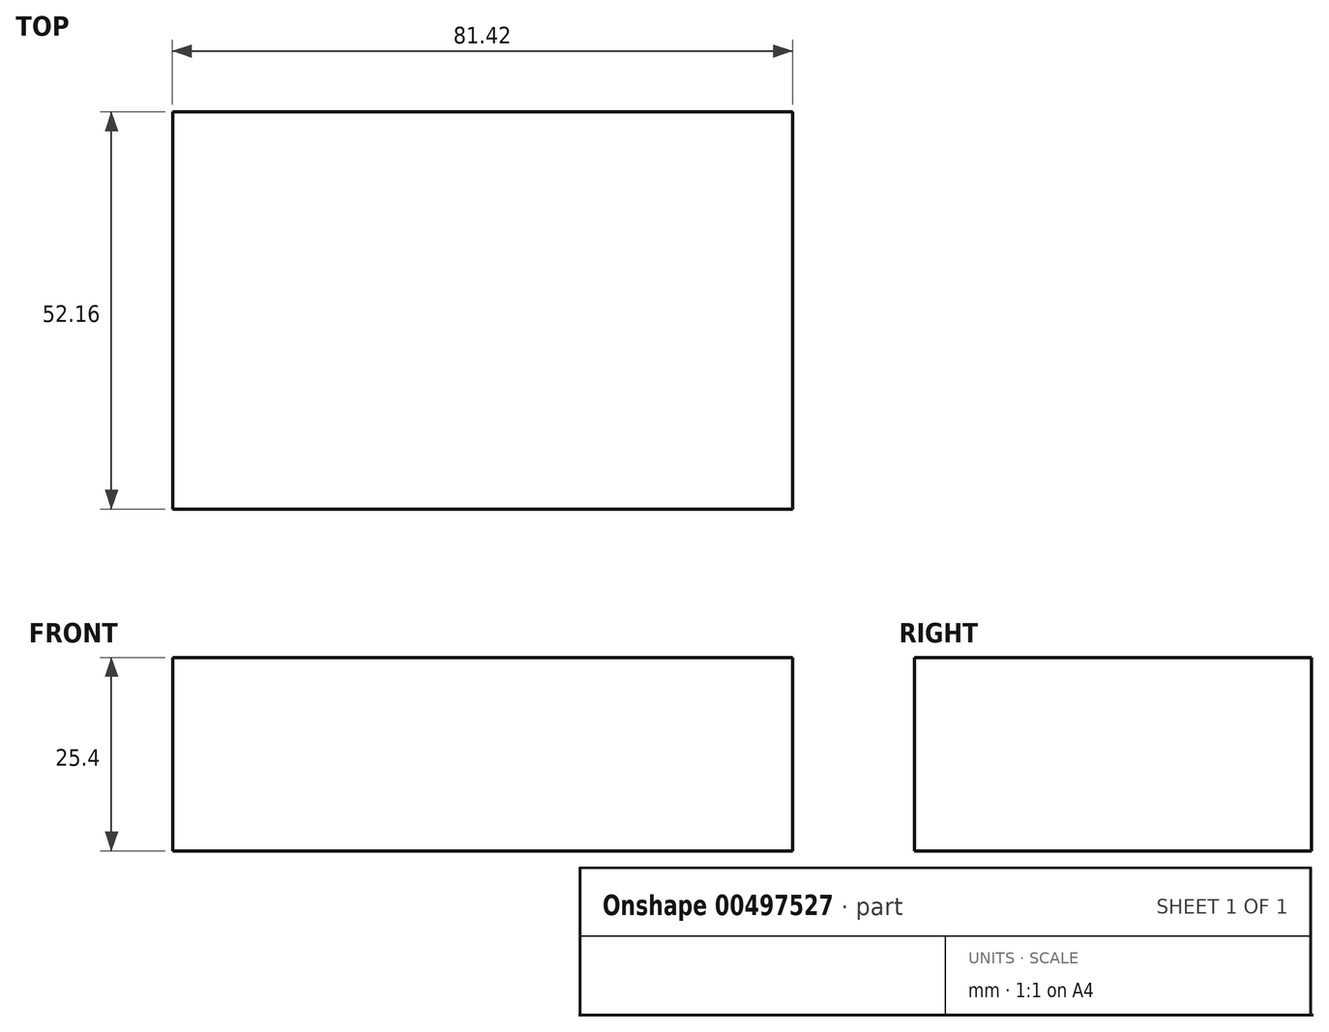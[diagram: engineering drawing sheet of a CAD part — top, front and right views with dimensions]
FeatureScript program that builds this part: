
annotation { "Feature Type Name" : "Feature", "Feature Type Description" : "" }
export const myFeature = defineFeature(function(context is Context, id is Id, definition is map)
    precondition{}
    {
        {
            var Q0;
            Q0=qCreatedBy(makeId("Top.planeOp"),FACE);
            var sketch = newSketch(context, id + "F0", { "sketchPlane" : qUnion([Q0])});
            skLineSegment(sketch, "E0.bottom", {"start": v(40.7, -26.08) * mm, "end": v(-40.7, -26.08) * mm});
            skLineSegment(sketch, "E0.top", {"start": v(40.7, 26.08) * mm, "end": v(-40.7, 26.08) * mm});
            skLineSegment(sketch, "E0.left", {"start": v(40.7, -26.08) * mm, "end": v(40.7, 26.08) * mm});
            skLineSegment(sketch, "E0.right", {"start": v(-40.7, -26.08) * mm, "end": v(-40.7, 26.08) * mm});
            skPoint(sketch, "E0.middle", {"position": v(0, 0) * mm});
            skSolve(sketch);
        }
        {
            var Q0;
            Q0 = qSketchRegion(id + "F0", true);
            extrude(context, id + "F1", {"entities" : qUnion([Q0]), "depth" : 25.4 * mm});
        }
    });
